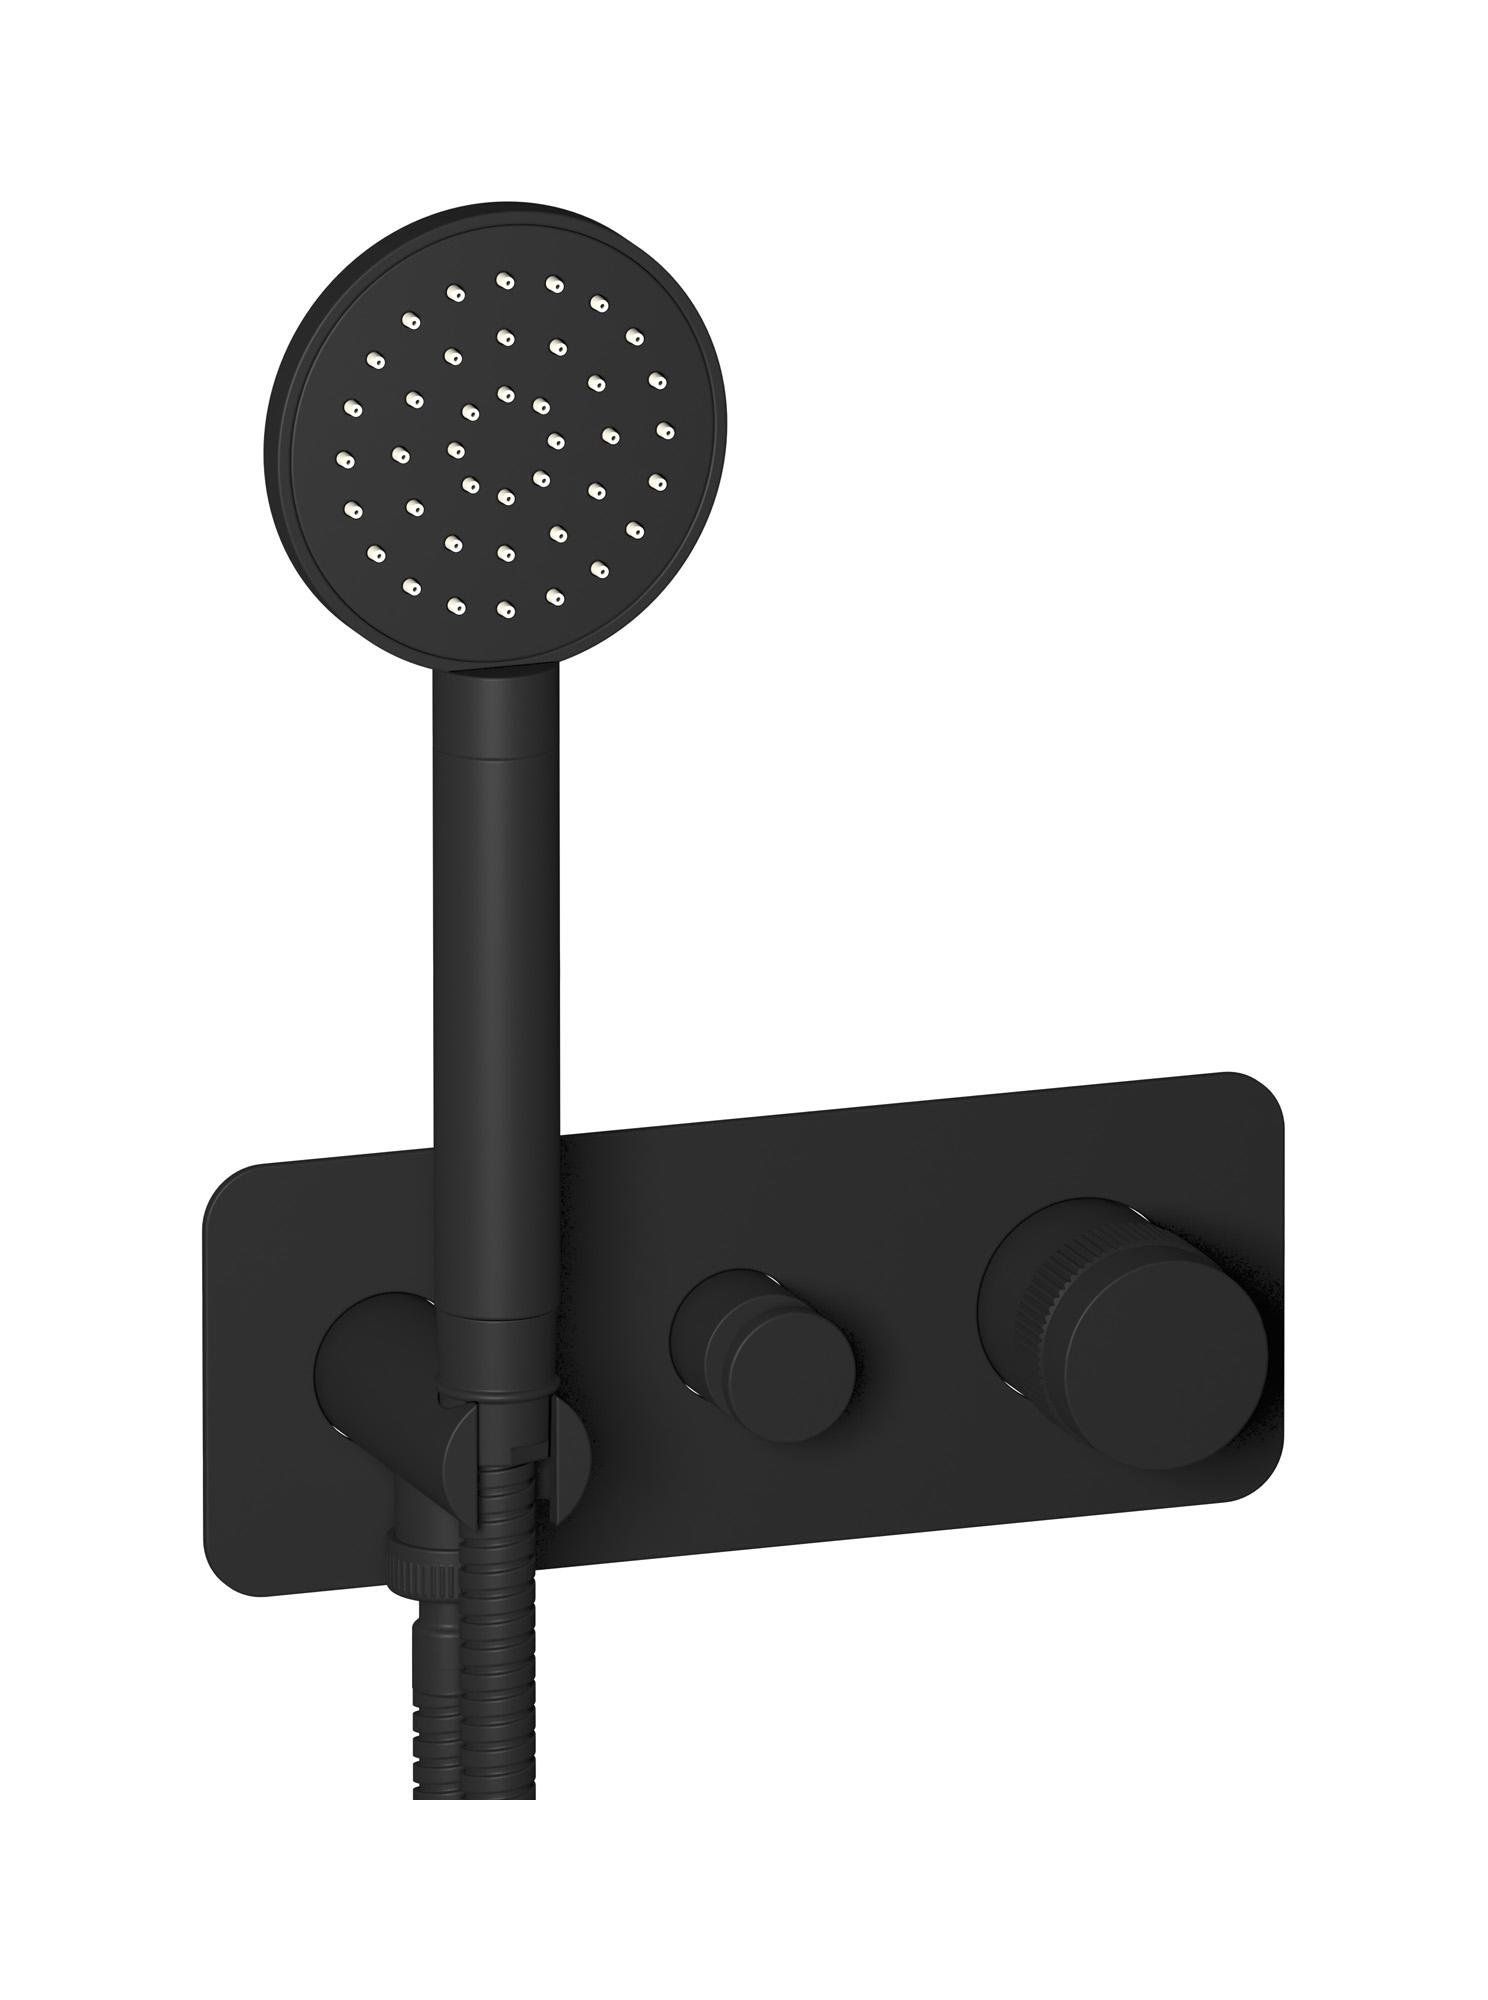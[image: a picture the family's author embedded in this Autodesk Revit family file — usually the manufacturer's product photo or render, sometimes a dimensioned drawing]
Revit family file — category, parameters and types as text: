
# Revit family: RX313
name_source: partatom
category: Apparecchi idraulici
units: mm (PartAtom-declared; Revit-internal decimal feet)

## family parameters
Basato su piano di lavoro = No
Condiviso = No
Mantieni orientamento annotazione = No
Numero OmniClass = 23.45.55.17
Punto di calcolo locali = No
Quota connettore circolare = Usa diametro
Sempre verticale = Sì
Taglio con vuoti quando caricato = No
Tipo di parte = Normale
Titolo OmniClass = Mixing Faucets

## types (12) — shared parameters
Cold water inlet = 10 mm  [stored 0.0328084 ft]
Commenti sul tipo = 2 ways wall shower hydroprogressive mixer complete with shower kit
Connessione CW = No
Connessione HW = No
Connessione di scarico = No
Connessione di ventilazione = No
Descrizione = 2 ways wall shower hydroprogressive mixer complete with shower kit
Hot water inlet = 10 mm  [stored 0.0328084 ft]
Produttore = IB Rubinetterie S.p.A.
URL = https://www.weareib.it
zero-valued in all types: Prospetto di default

## per-type parameters (varying)
| type | Finishes surface | Immagine tipo | Modello |
| Chrome | IB_Chrome | RX313CC.jpg | RX313CC |
| Black Chrome | IB_Black chrome | RX313CF.jpg | RX313CF |
| Brushed Black Chrome | IB_Brushed black chrome | RX313CS.jpg | RX313CS |
| Pale Gold | IB_Pale gold | RX313II.jpg | RX313II |
| Brushed Pale Gold | IB_brushed pale gold | RX313IS.jpg | RX313IS |
| Matt Black | IB_matt black | RX313NP.jpg | RX313NP |
| Natural Brass | IB_Brass | RX313ON.jpg | RX313ON |
| Gold | IB_gold | RX313OO.jpg | RX313OO |
| Brushed Gold | IB_brushed gold | RX313OS.jpg | RX313OS |
| Rose Gold | IB_Rose gold | RX313RS.jpg | RX313RS |
| Brushed Rose Gold | IB_Brushed rose gold | RX313SR.jpg | RX313SR |
| Brushed Nickel | IB_Brushed nickel | RX313SS.jpg | RX313SS |

note: [stored X ft] marks values corroborated as IEEE doubles in the binary element streams (Revit-internal decimal feet)
